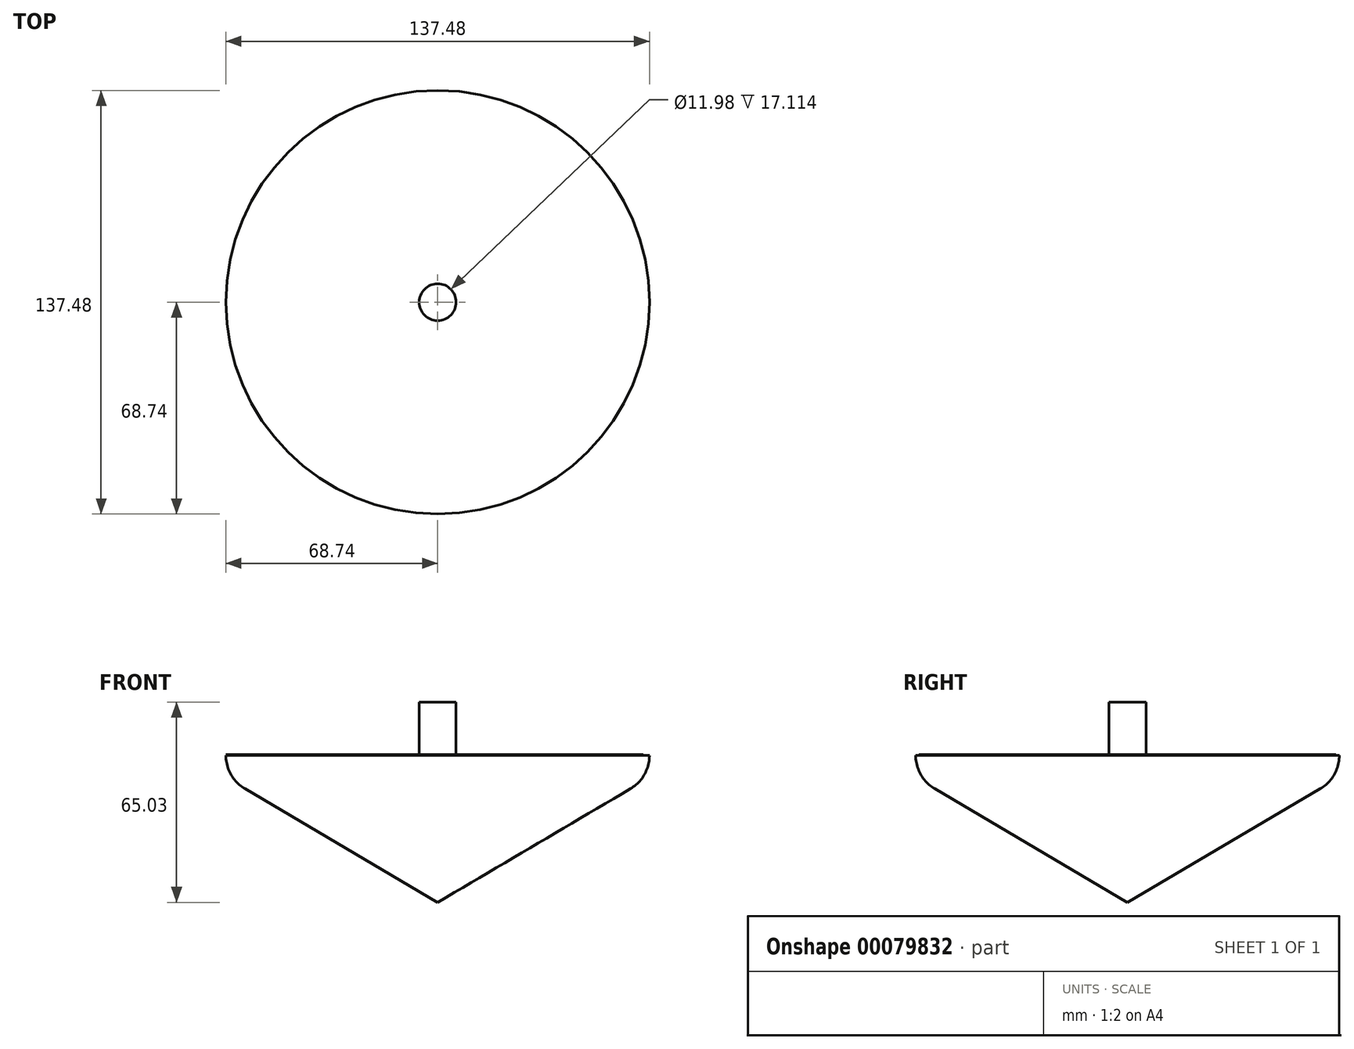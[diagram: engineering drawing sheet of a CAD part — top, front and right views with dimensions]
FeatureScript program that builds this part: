
annotation { "Feature Type Name" : "Feature", "Feature Type Description" : "" }
export const myFeature = defineFeature(function(context is Context, id is Id, definition is map)
    precondition{}
    {
        {
            var Q0;
            Q0=qCreatedBy(makeId("Front.planeOp"),FACE);
            var sketch = newSketch(context, id + "F0", { "sketchPlane" : qUnion([Q0])});
            skLineSegment(sketch, "E0", {"start": v(0, 9.84) * mm, "end": v(-6, 9.84) * mm});
            skLineSegment(sketch, "E1", {"start": v(-6, 9.84) * mm, "end": v(-6, -7.27) * mm});
            skLineSegment(sketch, "E2", {"start": v(-6, -7.27) * mm, "end": v(-68.74, -7.27) * mm});
            skLineSegment(sketch, "E3", {"start": v(-68.74, -7.27) * mm, "end": v(-68.74, -7.53) * mm});
            skLineSegment(sketch, "E4", {"start": v(-62.57, -18.32) * mm, "end": v(0, -55.2) * mm});
            skLineSegment(sketch, "E5", {"start": v(0, 9.84) * mm, "end": v(0, -55.2) * mm});
            skPoint(sketch, "E6.visualSharp", {"position": v(-68.74, -14.69) * mm});
            skArc(sketch, "E6.filletArc", {"start": v(-68.74, -7.53) * mm, "mid": v(-67.1, -13.75) * mm, "end": v(-62.57, -18.32) * mm});
            skSolve(sketch);
        }
        {
            var Q0;
            Q0=sQuery(id+"F0.wireOp",EDGE,"E0");
            var Q1;
            Q1=sQuery(id+"F0.wireOp",EDGE,"E1");
            var Q2;
            Q2=sQuery(id+"F0.wireOp",EDGE,"E2");
            var Q3;
            Q3=sQuery(id+"F0.wireOp",EDGE,"E6.filletArc");
            var Q4;
            Q4=sQuery(id+"F0.wireOp",EDGE,"E4");
            var Q5;
            Q5=sQuery(id+"F0.wireOp",EDGE,"E5");
            revolve(context, id + "F1", {"bodyType" : ToolBodyType.SURFACE, "surfaceEntities" : qUnion([Q0, Q1, Q2, Q3, Q4]), "axis" : qUnion([Q5]), "revolveType" : RevolveType.FULL});
        }
    });
